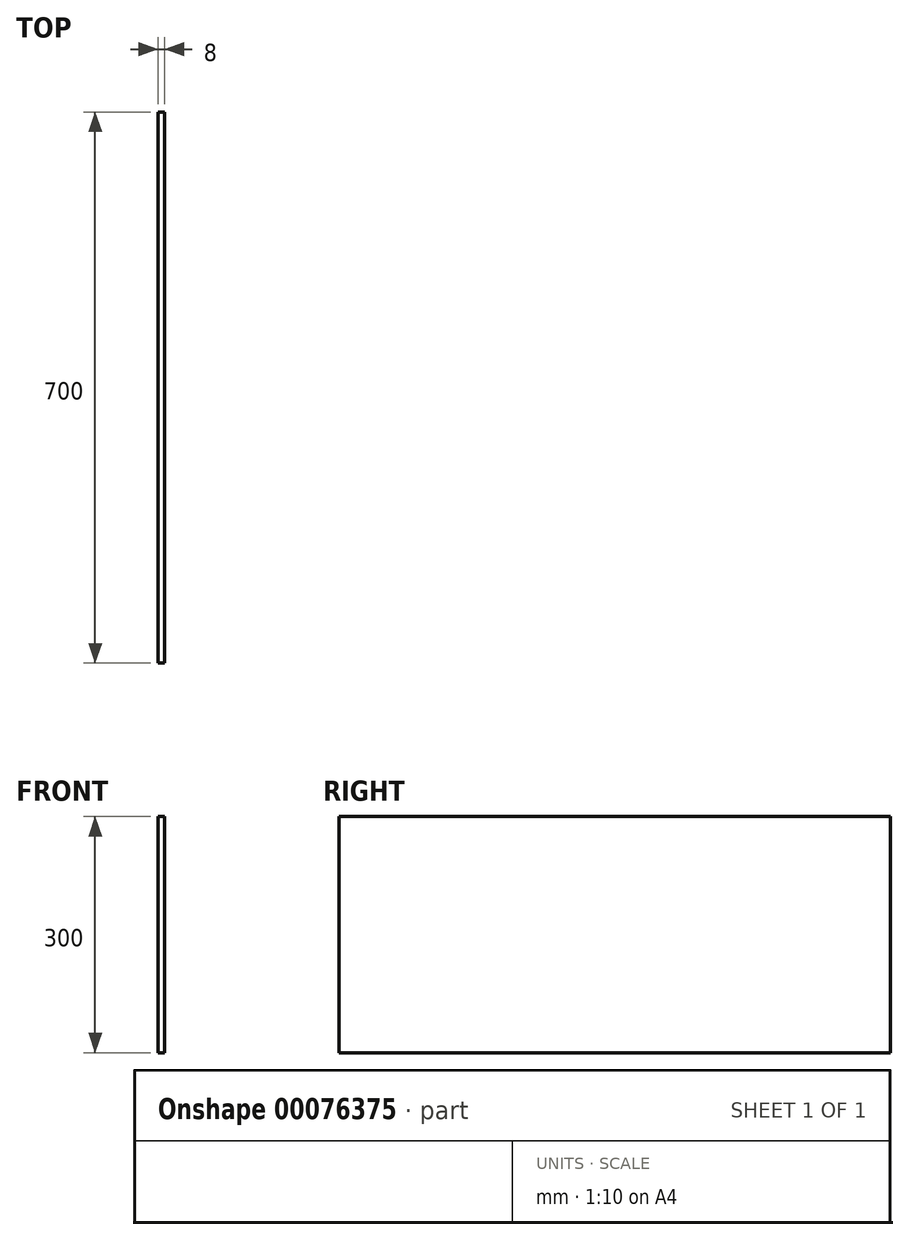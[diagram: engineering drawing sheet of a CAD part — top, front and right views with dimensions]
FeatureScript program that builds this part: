
annotation { "Feature Type Name" : "Feature", "Feature Type Description" : "" }
export const myFeature = defineFeature(function(context is Context, id is Id, definition is map)
    precondition{}
    {
        {
            var Q0;
            Q0=qCreatedBy(makeId("Right.planeOp"),FACE);
            var sketch = newSketch(context, id + "F0", { "sketchPlane" : qUnion([Q0])});
            skLineSegment(sketch, "E0.bottom", {"start": v(0, 0) * mm, "end": v(700, 0) * mm});
            skLineSegment(sketch, "E0.top", {"start": v(0, 300) * mm, "end": v(700, 300) * mm});
            skLineSegment(sketch, "E0.left", {"start": v(0, 0) * mm, "end": v(0, 300) * mm});
            skLineSegment(sketch, "E0.right", {"start": v(700, 0) * mm, "end": v(700, 300) * mm});
            skSolve(sketch);
        }
        {
            var Q0;
            Q0 = qSketchRegion(id + "F0", true);
            extrude(context, id + "F1", {"entities" : qUnion([Q0]), "depth" : 8 * mm});
        }
    });
